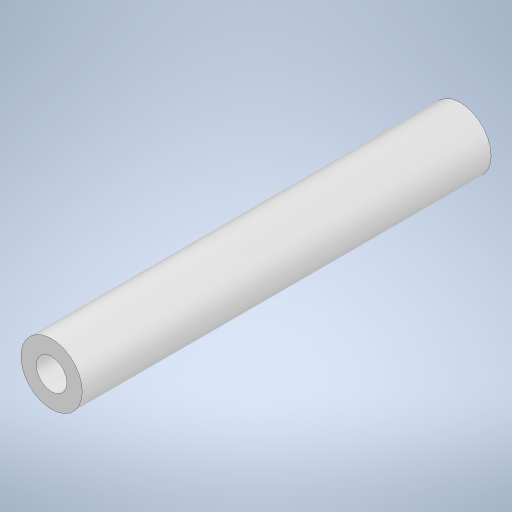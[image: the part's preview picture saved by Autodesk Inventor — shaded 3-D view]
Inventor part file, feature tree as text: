
AUTODESK INVENTOR PART (.ipt)
format: ipt  version: 2023 (Build 270158000, 158)  size: 247,808 bytes
history: native  units: mm
features: extrude x3, sketch x3
ambient origin geometry x8: Origin, YZ Plane, XZ Plane, XY Plane, X Axis, Y Axis, Z Axis, Center Point
bodies: Solid1 (feature_tree)
feature tree (6):
  extrude  "Extrusion1"  Depth=6.0mm
  extrude  "押し出し2"  Depth=40.0mm TaperAngle=0.0deg
  extrude  "押し出し3"  Depth=3.0mm
  sketch  "Sketch1"  dims[d0=2.5mm d1=6.0mm d2=40.0mm d3=0.0mm d4=3.0mm d5=6.0mm d6=0.0mm d7=6.0mm d8=0.0mm]
  sketch  "スケッチ2"
  sketch  "スケッチ3"
